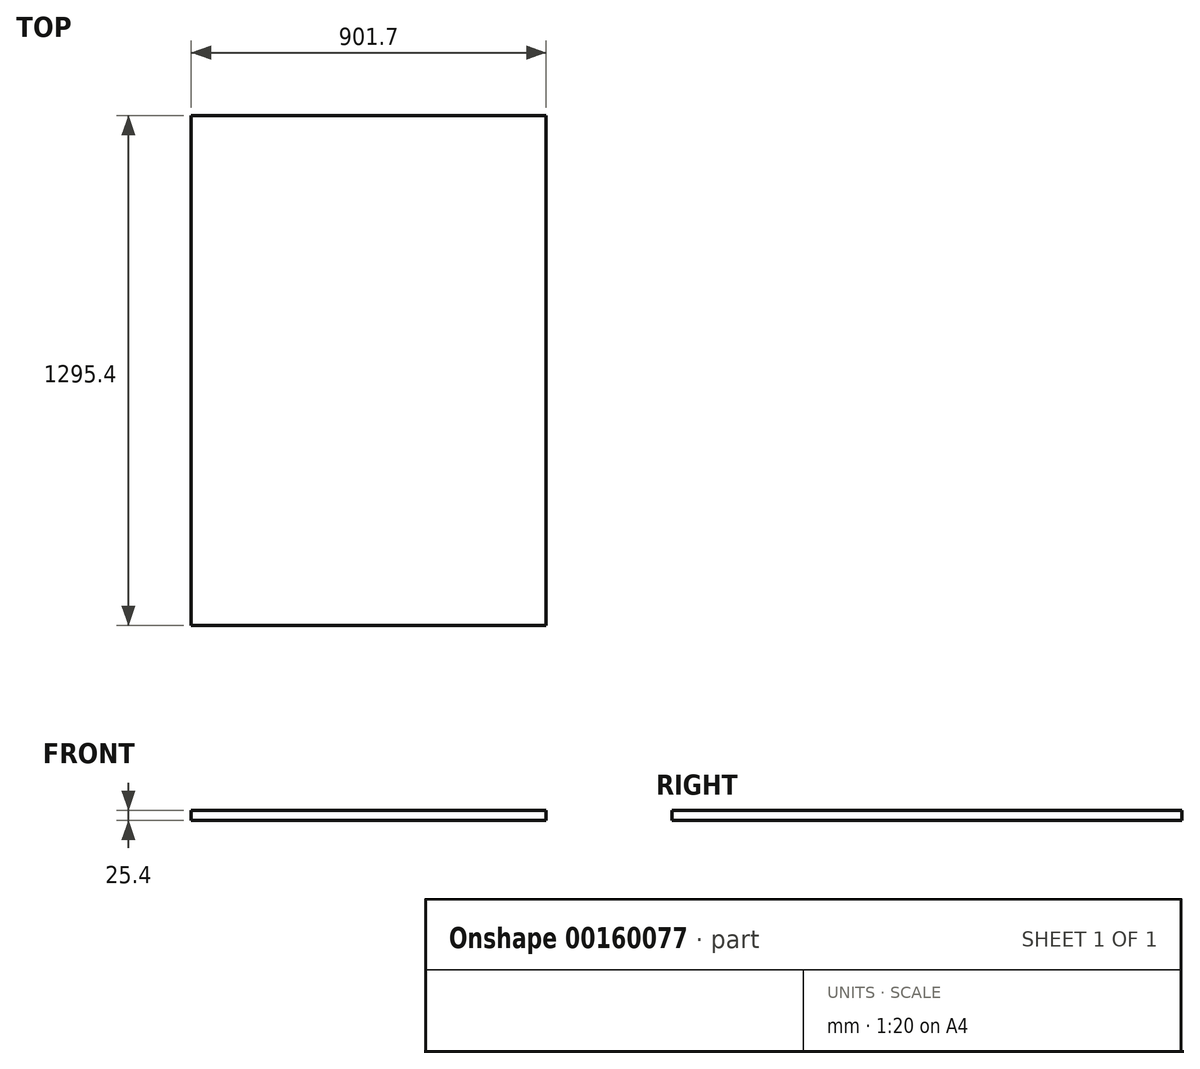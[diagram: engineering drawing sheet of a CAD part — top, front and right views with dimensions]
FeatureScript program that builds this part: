
annotation { "Feature Type Name" : "Feature", "Feature Type Description" : "" }
export const myFeature = defineFeature(function(context is Context, id is Id, definition is map)
    precondition{}
    {
        {
            var Q0;
            Q0=qCreatedBy(makeId("Top.planeOp"),FACE);
            var sketch = newSketch(context, id + "F0", { "sketchPlane" : qUnion([Q0])});
            skLineSegment(sketch, "E0.bottom", {"start": v(-491, 911.43) * mm, "end": v(410.7, 911.43) * mm});
            skLineSegment(sketch, "E0.top", {"start": v(-491, -383.97) * mm, "end": v(410.7, -383.97) * mm});
            skLineSegment(sketch, "E0.left", {"start": v(-491, 911.43) * mm, "end": v(-491, -383.97) * mm});
            skLineSegment(sketch, "E0.right", {"start": v(410.7, 911.43) * mm, "end": v(410.7, -383.97) * mm});
            skSolve(sketch);
        }
        {
            var Q0;
            Q0=makeQuery(id+"F0.imprint","IMPRINT",FACE,{"disambiguationData":[TD([[makeQuery(id+"F0.imprint","IMPRINT",EDGE,{"derivedFrom":sQuery(id+"F0.wireOp",EDGE,"E0.bottom")}),-1.0]])]});
            extrude(context, id + "F1", {"entities" : qUnion([Q0]), "depth" : 25.4 * mm});
        }
    });
